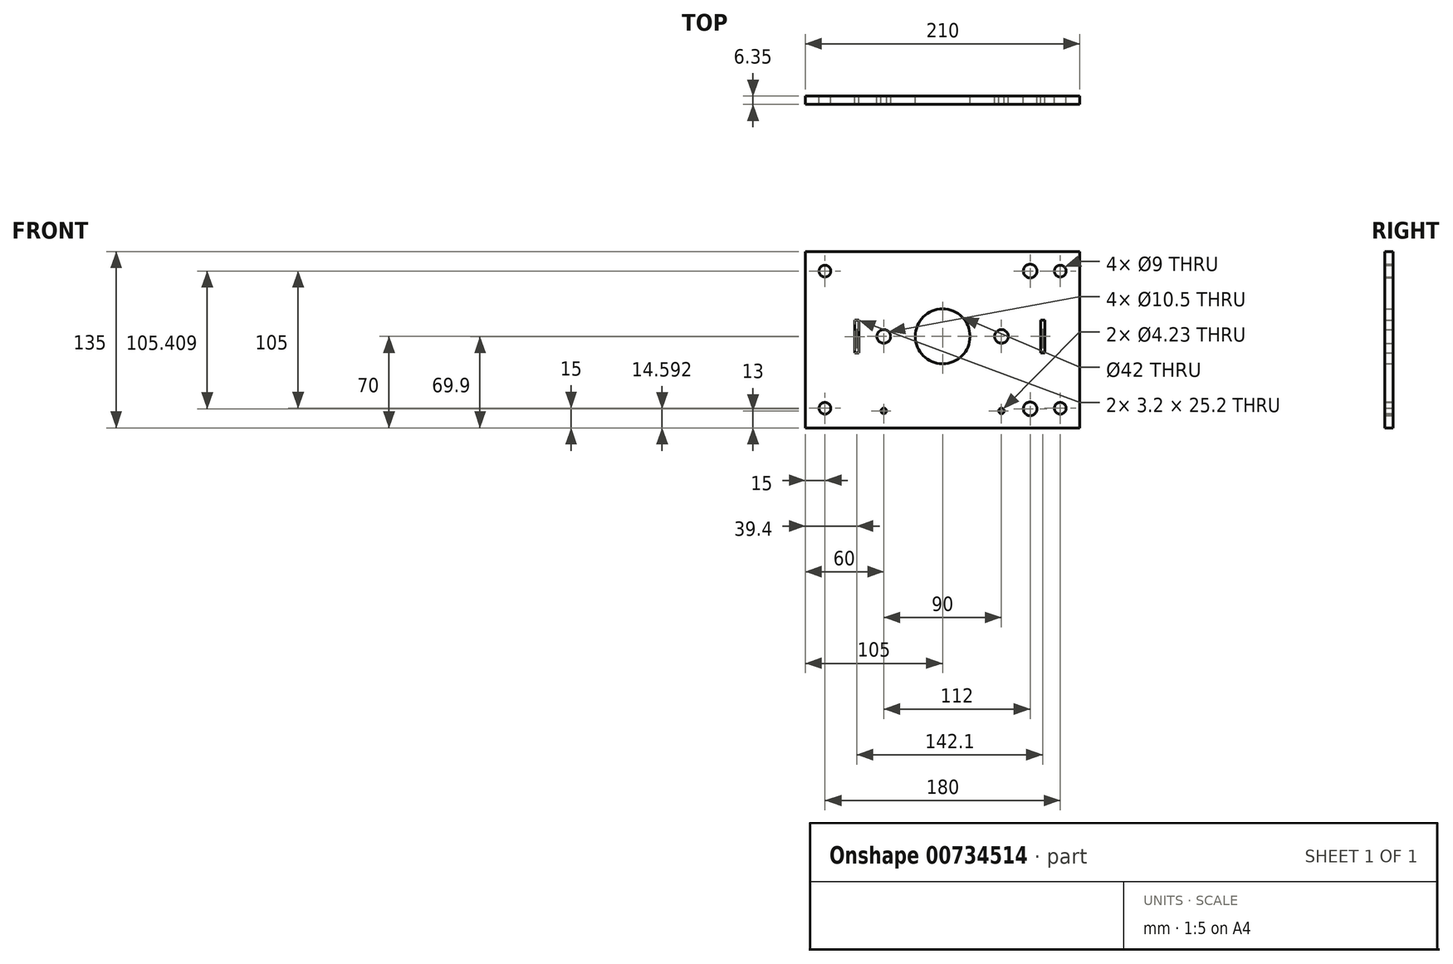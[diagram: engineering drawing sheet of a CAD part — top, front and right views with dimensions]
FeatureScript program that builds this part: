
annotation { "Feature Type Name" : "Feature", "Feature Type Description" : "" }
export const myFeature = defineFeature(function(context is Context, id is Id, definition is map)
    precondition{}
    {
        {
            var Q0;
            Q0=qCreatedBy(makeId("Front.planeOp"),FACE);
            var sketch = newSketch(context, id + "F0", { "sketchPlane" : qUnion([Q0])});
            skLineSegment(sketch, "E0", {"start": v(-64, -10.2) * mm, "end": v(-64, 15) * mm});
            skLineSegment(sketch, "E1", {"start": v(-64, 15) * mm, "end": v(-67.2, 15) * mm});
            skLineSegment(sketch, "E2", {"start": v(-67.2, 15) * mm, "end": v(-67.2, -10.2) * mm});
            skLineSegment(sketch, "E3", {"start": v(-67.2, -10.2) * mm, "end": v(-64, -10.2) * mm});
            skLineSegment(sketch, "E4", {"start": v(-105, 67.5) * mm, "end": v(105, 67.5) * mm});
            skLineSegment(sketch, "E5", {"start": v(105, 67.5) * mm, "end": v(105, -67.5) * mm});
            skLineSegment(sketch, "E6", {"start": v(105, -67.5) * mm, "end": v(-105, -67.5) * mm});
            skLineSegment(sketch, "E7", {"start": v(-105, -67.5) * mm, "end": v(-105, 67.5) * mm});
            skLineSegment(sketch, "E8", {"start": v(74.9, 15.1) * mm, "end": v(74.9, -10.1) * mm});
            skLineSegment(sketch, "E9", {"start": v(74.9, -10.1) * mm, "end": v(78.1, -10.1) * mm});
            skLineSegment(sketch, "E10", {"start": v(78.1, -10.1) * mm, "end": v(78.1, 15.1) * mm});
            skLineSegment(sketch, "E11", {"start": v(78.1, 15.1) * mm, "end": v(74.9, 15.1) * mm});
            skCircle(sketch, "E12", {"center": v(-45, 2.5) * mm, "radius": 5.25 * mm});
            skCircle(sketch, "E13", {"center": v(45, -54.5) * mm, "radius": 2.12 * mm});
            skCircle(sketch, "E14", {"center": v(-45, -54.5) * mm, "radius": 2.12 * mm});
            skCircle(sketch, "E15", {"center": v(45, 2.5) * mm, "radius": 5.25 * mm});
            skCircle(sketch, "E16", {"center": v(0, 2.5) * mm, "radius": 21 * mm});
            skCircle(sketch, "E17", {"center": v(67, 52.5) * mm, "radius": 5.25 * mm});
            skCircle(sketch, "E18", {"center": v(90, 52.5) * mm, "radius": 4.5 * mm});
            skCircle(sketch, "E19", {"center": v(-90, -52.5) * mm, "radius": 4.5 * mm});
            skCircle(sketch, "E20", {"center": v(-90, 52.5) * mm, "radius": 4.5 * mm});
            skCircle(sketch, "E21", {"center": v(90, -52.5) * mm, "radius": 4.5 * mm});
            skCircle(sketch, "E22", {"center": v(67, -52.9) * mm, "radius": 5.25 * mm});
            skSolve(sketch);
        }
        {
            var Q0;
            Q0 = qSketchRegion(id + "F0", true);
            extrude(context, id + "F1", {"entities" : qUnion([Q0]), "depth" : 6.35 * mm, "offsetDistance" : 25.4 * mm});
        }
    });
